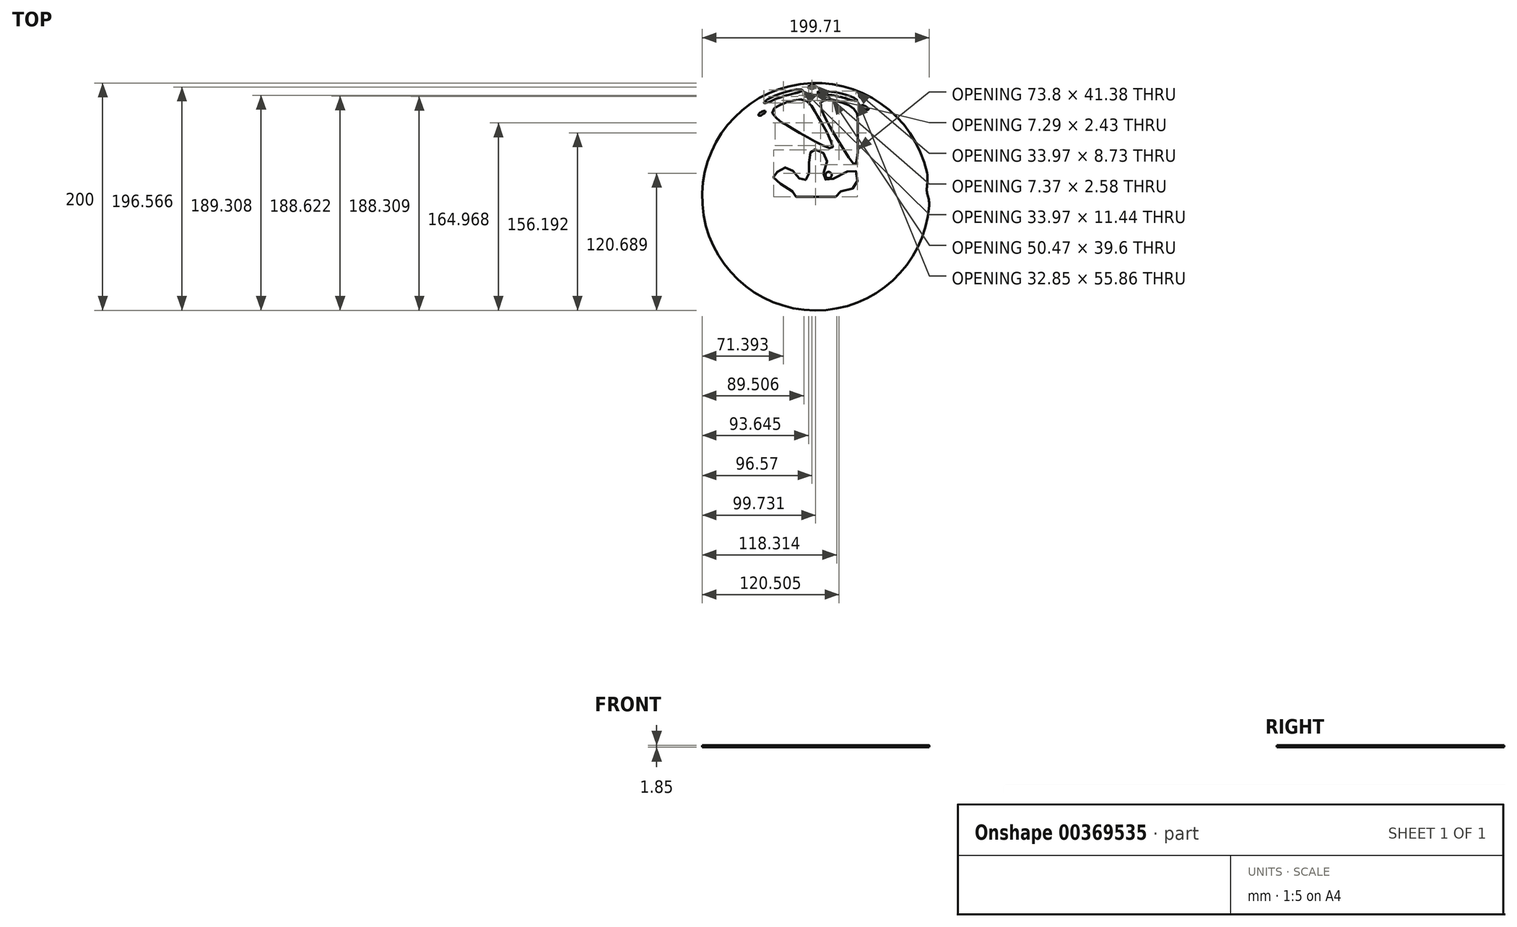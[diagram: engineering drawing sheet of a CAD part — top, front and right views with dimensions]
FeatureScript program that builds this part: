
annotation { "Feature Type Name" : "Feature", "Feature Type Description" : "" }
export const myFeature = defineFeature(function(context is Context, id is Id, definition is map)
    precondition{}
    {
        {
            var Q0;
            Q0=qCreatedBy(makeId("Top.planeOp"),FACE);
            var sketch = newSketch(context, id + "F0", { "sketchPlane" : qUnion([Q0])});
            skCircle(sketch, "E0", {"center": v(0, 0) * mm, "radius": 100 * mm});
            skSolve(sketch);
        }
        {
            var Q0;
            Q0 = qSketchRegion(id + "F0", true);
            extrude(context, id + "F1", {"entities" : qUnion([Q0]), "depth" : 1.85 * mm});
        }
        {
            var Q0;
            Q0=qCreatedBy(makeId("Top.planeOp"),FACE);
            var sketch = newSketch(context, id + "F2", { "sketchPlane" : qUnion([Q0])});
            skFitSpline(sketch, "E1", {"points": [v(-19.38, 84.77) * mm, v(-8.63, 84.56) * mm, v(-1.67, 76.6) * mm, v(3.06, 68.35) * mm, v(13.97, 47.56) * mm, v(14.31, 42.83) * mm, v(5.56, 45.43) * mm, v(-11.71, 54.73) * mm, v(-25.19, 62.69) * mm, v(-32.07, 66.92) * mm, v(-38.38, 74.95) * mm, v(-29.42, 81.62) * mm, v(-19.38, 84.77) * mm]});
            skFitSpline(sketch, "E2", {"points": [v(4.08, 83.02) * mm, v(10.34, 85.27) * mm, v(19.63, 83.7) * mm, v(28.63, 80.68) * mm, v(35.57, 74.9) * mm, v(36.94, 66) * mm, v(36.84, 45.47) * mm, v(36.55, 35.5) * mm, v(34.69, 28.35) * mm, v(30.68, 31.97) * mm, v(18.16, 51.92) * mm, v(10.63, 64.93) * mm, v(4.08, 83.02) * mm]});
            skCircle(sketch, "E3", {"center": v(11.21, 19.1) * mm, "radius": 2.74 * mm});
            skFitSpline(sketch, "E4", {"points": [v(1.33, 91.88) * mm, v(3.92, 92.97) * mm, v(20.65, 91.15) * mm, v(33.86, 86.8) * mm, v(36.3, 84.47) * mm, v(32.15, 84.78) * mm, v(24.8, 87.06) * mm, v(11.43, 89.65) * mm, v(3.56, 90.69) * mm, v(1.33, 91.88) * mm]});
            skEllipse(sketch, "E5", {"center": v(-6.35, 89.3) * mm, "majorRadius": 3.66 * mm, "minorRadius": 1.22 * mm, "majorAxis": v(1, 0.08)});
            skEllipse(sketch, "E6", {"center": v(-3.43, 96.57) * mm, "majorRadius": 3.69 * mm, "minorRadius": 1.3 * mm, "majorAxis": v(1, 0.05)});
            skFitSpline(sketch, "E7", {"points": [v(-45.6, 82.59) * mm, v(-43.93, 84.78) * mm, v(-33.52, 89.86) * mm, v(-22.17, 93.37) * mm, v(-13.05, 94.32) * mm, v(-11.62, 93.66) * mm, v(-13.9, 92.28) * mm, v(-21.27, 90.43) * mm, v(-35.28, 85.92) * mm, v(-43.21, 82.64) * mm, v(-45.6, 82.59) * mm]});
            skSolve(sketch);
        }
        {
            var Q0;
            Q0 = qSketchRegion(id + "F2", true);
            extrude(context, id + "F3", {"entities" : qUnion([Q0]), "operationType" : NewBodyOperationType.REMOVE, "endBound" : BoundingType.THROUGH_ALL, "depth" : 25.4 * mm});
        }
        {
            var Q0;
            Q0=qCreatedBy(makeId("Right.planeOp"),FACE);
            var sketch = newSketch(context, id + "F4", { "sketchPlane" : qUnion([Q0])});
            skLineSegment(sketch, "E8", {"start": v(0, 95.36) * mm, "end": v(0, -57.75) * mm, "construction": true});
            skSolve(sketch);
        }
        {
            var Q0;
            Q0=qCreatedBy(makeId("Top.planeOp"),FACE);
            var sketch = newSketch(context, id + "F5", { "sketchPlane" : qUnion([Q0])});
            skEllipse(sketch, "E9", {"center": v(41.45, 87.42) * mm, "majorRadius": 3.57 * mm, "minorRadius": 1.2 * mm, "majorAxis": v(0.91, -0.4)});
            skEllipse(sketch, "E10", {"center": v(43.1, 78.52) * mm, "majorRadius": 3.63 * mm, "minorRadius": 1.26 * mm, "majorAxis": v(0.88, -0.47)});
            skEllipse(sketch, "E11", {"center": v(-47.44, 73.48) * mm, "majorRadius": 3.63 * mm, "minorRadius": 1.22 * mm, "majorAxis": v(0.85, 0.53)});
            skFitSpline(sketch, "E12", {"points": [v(97.75, 21.08) * mm, v(97.65, 5.22) * mm, v(99.68, -7.96) * mm], "startDerivative": vector(7.26, -40.7) * mm, "endDerivative": vector(-1.85, -36.8) * mm});
            skArc(sketch, "E13", {"start": v(99.68, -7.96) * mm, "mid": v(99.78, 6.63) * mm, "end": v(97.75, 21.08) * mm});
            skSolve(sketch);
        }
        {
            var Q0;
            Q0=qCreatedBy(makeId("Right.planeOp"),FACE);
            var sketch = newSketch(context, id + "F6", { "sketchPlane" : qUnion([Q0])});
            skLineSegment(sketch, "E14", {"start": v(0, 52.55) * mm, "end": v(0, -107.98) * mm, "construction": true});
            skSolve(sketch);
        }
        {
            var Q0;
            Q0 = qSketchRegion(id + "F5", true);
            extrude(context, id + "F7", {"entities" : qUnion([Q0]), "operationType" : NewBodyOperationType.REMOVE, "endBound" : BoundingType.THROUGH_ALL, "depth" : 25.4 * mm});
        }
        {
            var Q0;
            Q0=qCreatedBy(makeId("Top.planeOp"),FACE);
            var sketch = newSketch(context, id + "F8", { "sketchPlane" : qUnion([Q0])});
            skFitSpline(sketch, "E15", {"points": [v(-17.56, 0) * mm, v(-18.46, 3.14) * mm, v(-34.03, 13.42) * mm, v(-37.43, 18.35) * mm, v(-32.76, 22.89) * mm, v(-25.05, 25.87) * mm, v(-17.63, 19.91) * mm, v(-12.13, 14.5) * mm, v(-7.37, 15.88) * mm, v(-6.08, 24.13) * mm, v(-5.27, 36.98) * mm, v(-2.88, 41.63) * mm, v(3.45, 40.02) * mm, v(9.96, 34.2) * mm, v(6.38, 19.36) * mm, v(8.3, 15.33) * mm, v(13.44, 14.87) * mm, v(33.32, 23.94) * mm, v(36.35, 18.35) * mm, v(34.8, 8.73) * mm, v(20.86, 4.34) * mm, v(17.56, 0) * mm], "startDerivative": vector(0, 131.9) * mm, "endDerivative": vector(0, -132.28) * mm});
            skLineSegment(sketch, "E16", {"start": v(-17.56, 0) * mm, "end": v(17.56, 0) * mm});
            skSolve(sketch);
        }
        {
            var Q0;
            Q0=qCreatedBy(makeId("Right.planeOp"),FACE);
            var sketch = newSketch(context, id + "F9", { "sketchPlane" : qUnion([Q0])});
            skLineSegment(sketch, "E17", {"start": v(0, 42.1) * mm, "end": v(0, -91.74) * mm, "construction": true});
            skSolve(sketch);
        }
        {
            var Q0;
            Q0 = qSketchRegion(id + "F8", true);
            extrude(context, id + "F10", {"entities" : qUnion([Q0]), "operationType" : NewBodyOperationType.REMOVE, "endBound" : BoundingType.THROUGH_ALL, "depth" : 25.4 * mm});
        }
    });
